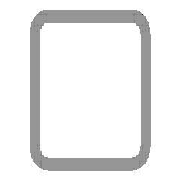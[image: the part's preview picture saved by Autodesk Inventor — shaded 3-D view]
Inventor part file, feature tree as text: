
AUTODESK INVENTOR PART (.ipt)
format: ipt  version: 2021 (Build 250183000, 183)  size: 142,848 bytes
history: native  units: mm (DEFAULTED — no unit token found)
features: other x5, sketch x3, extrude x1, split x1, plane x1
ambient origin geometry x8: Origin, YZ Plane, XZ Plane, XY Plane, X Axis, Y Axis, Z Axis, Center Point
bodies: Solid1 (feature_tree)
feature tree (11):
  parser-record x1  (decoder bookkeeping rows leaked as tree rows — omitted from the tree; the rows remain in map.json)
  other  "Driven Length"
  other  "Plano inicial"
  other  "Plano final"
  extrude  "Corpo"  TaperAngle=0.0deg  [1 undecoded]
  other  "Plano de trabalho4"
  split  "Dividir1"
  sketch  "Esboço"  dims[d11=50.8mm d12=4.7625mm d13=-34.077676mm d14=1000.0mm d15=25.4mm d16=25.4mm d17=9.525mm d18=90.0deg d19=1034.077676mm]
  sketch  "Sketch3"  dims[d3=1030.799585mm d4=0.0mm]
  plane  "Work Plane3"
  sketch  "Sketch4"  dims[d10=50.8mm]
note: 1 required parameter value undecoded (feature->parameter linkage not recoverable at this tier; creation-order binding heuristic only, values carry confidence <= 0.55)
